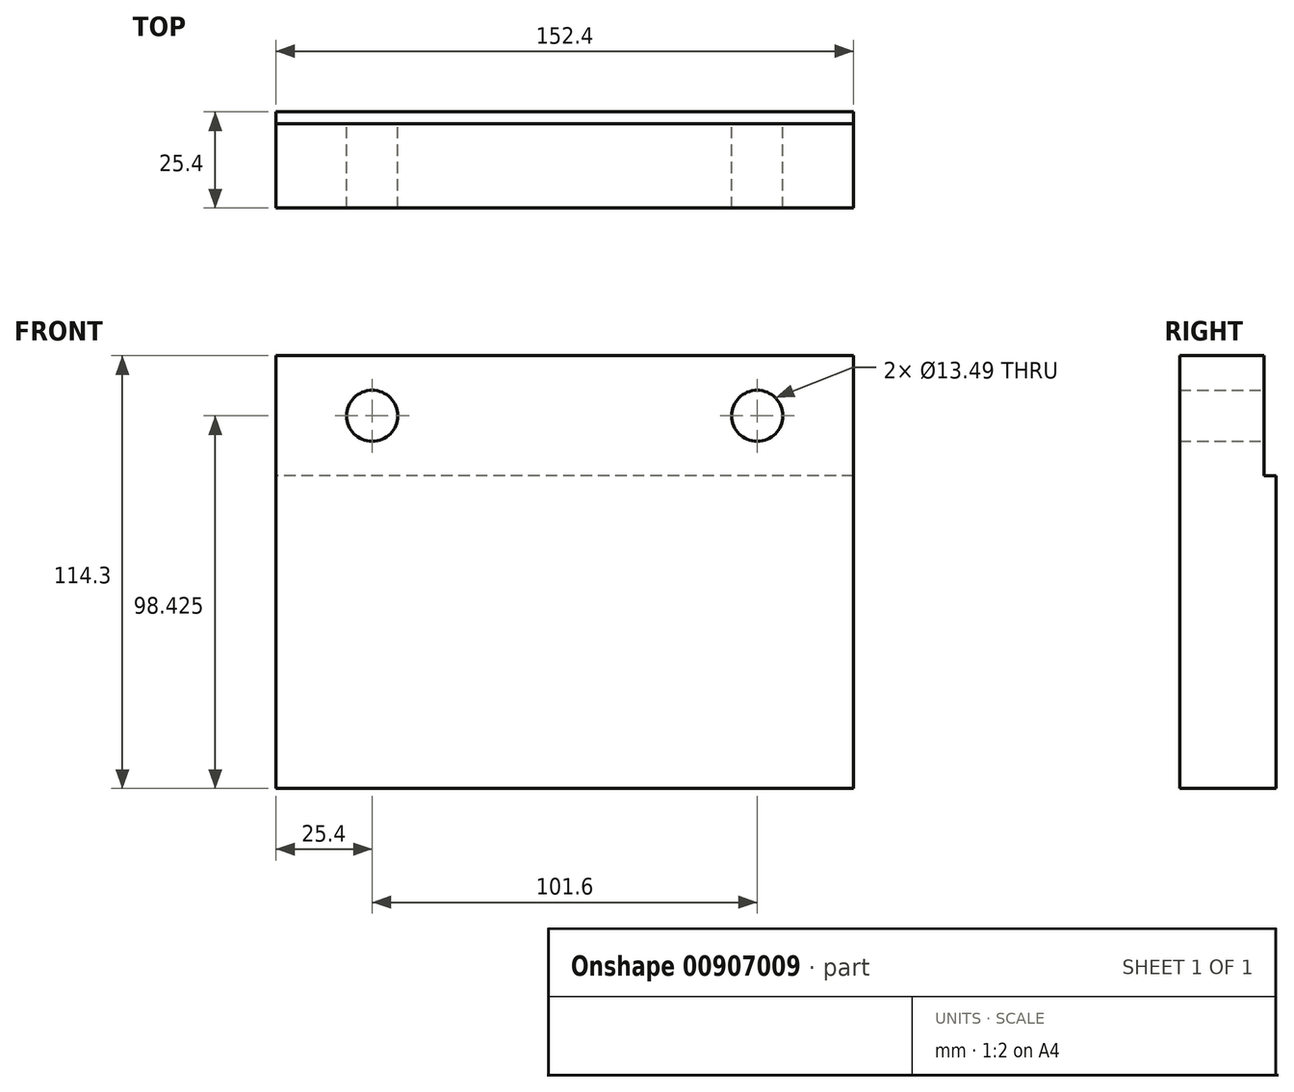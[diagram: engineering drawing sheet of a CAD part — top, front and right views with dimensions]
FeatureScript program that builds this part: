
annotation { "Feature Type Name" : "Feature", "Feature Type Description" : "" }
export const myFeature = defineFeature(function(context is Context, id is Id, definition is map)
    precondition{}
    {
        {
            var Q0;
            Q0=qCreatedBy(makeId("Front.planeOp"),FACE);
            var sketch = newSketch(context, id + "F0", { "sketchPlane" : qUnion([Q0])});
            skLineSegment(sketch, "E0.bottom", {"start": v(76.2, 57.15) * mm, "end": v(-76.2, 57.15) * mm});
            skLineSegment(sketch, "E0.top", {"start": v(76.2, -57.15) * mm, "end": v(-76.2, -57.15) * mm});
            skLineSegment(sketch, "E0.left", {"start": v(76.2, 57.15) * mm, "end": v(76.2, -57.15) * mm});
            skLineSegment(sketch, "E0.right", {"start": v(-76.2, 57.15) * mm, "end": v(-76.2, -57.15) * mm});
            skPoint(sketch, "E0.middle", {"position": v(0, 0) * mm});
            skSolve(sketch);
        }
        {
            var Q0;
            Q0=makeQuery(id+"F0.imprint","IMPRINT",FACE,{"disambiguationData":[TD([[makeQuery(id+"F0.imprint","IMPRINT",EDGE,{"derivedFrom":sQuery(id+"F0.wireOp",EDGE,"E0.bottom")}),1.0]])]});
            extrude(context, id + "F1", {"entities" : qUnion([Q0]), "depth" : 25.4 * mm, "offsetDistance" : 25.4 * mm});
        }
        {
            var Q0;
            Q0=makeQuery(id+"F1.opExtrude","CAP_FACE",FACE,{"disambiguationData":[OSD([sQuery(id+"F0.wireOp",EDGE,"E0.bottom"),sQuery(id+"F0.wireOp",EDGE,"E0.top"),sQuery(id+"F0.wireOp",EDGE,"E0.left"),sQuery(id+"F0.wireOp",EDGE,"E0.right")])],"isStart":true});
            var sketch = newSketch(context, id + "F2", { "sketchPlane" : qUnion([Q0])});
            skLineSegment(sketch, "E1.bottom", {"start": v(-76.2, 57.15) * mm, "end": v(76.2, 57.15) * mm});
            skLineSegment(sketch, "E1.top", {"start": v(-76.2, 25.4) * mm, "end": v(76.2, 25.4) * mm});
            skLineSegment(sketch, "E1.left", {"start": v(-76.2, 57.15) * mm, "end": v(-76.2, 25.4) * mm});
            skLineSegment(sketch, "E1.right", {"start": v(76.2, 57.15) * mm, "end": v(76.2, 25.4) * mm});
            skSolve(sketch);
        }
        {
            var Q0;
            Q0=makeQuery(id+"F2.imprint","IMPRINT",FACE,{"disambiguationData":[TD([[makeQuery(id+"F2.imprint","IMPRINT",EDGE,{"derivedFrom":sQuery(id+"F2.wireOp",EDGE,"E1.bottom")}),-1.0]])]});
            extrude(context, id + "F3", {"entities" : qUnion([Q0]), "operationType" : NewBodyOperationType.REMOVE, "oppositeDirection" : true, "depth" : 3.17 * mm, "offsetDistance" : 25.4 * mm});
        }
        {
            var Q0;
            Q0=makeQuery(id+"F3.boolean.opBoolean","COPY",FACE,{"derivedFrom":makeQuery(id+"F3.opExtrude","CAP_FACE",FACE,{"disambiguationData":[OSD([sQuery(id+"F2.wireOp",EDGE,"E1.bottom"),sQuery(id+"F2.wireOp",EDGE,"E1.top"),sQuery(id+"F2.wireOp",EDGE,"E1.left"),sQuery(id+"F2.wireOp",EDGE,"E1.right")])],"isStart":false})});
            var sketch = newSketch(context, id + "F4", { "sketchPlane" : qUnion([Q0])});
            skLineSegment(sketch, "E2", {"start": v(-50.8, 41.28) * mm, "end": v(50.8, 41.28) * mm, "construction": true});
            skLineSegment(sketch, "E3", {"start": v(0, 57.15) * mm, "end": v(0, 41.28) * mm, "construction": true});
            skSolve(sketch);
        }
        {
            var Q0;
            Q0=sQuery(id+"F4.wireOp",VERTEX,"E2.end");
            var Q1;
            Q1=sQuery(id+"F4.wireOp",VERTEX,"E2.start");
            var Q2;
            Q2=makeQuery(id+"F1.opExtrude","SWEPT_BODY",BODY,{"disambiguationData":[OSD([sQuery(id+"F0.wireOp",EDGE,"E0.bottom"),sQuery(id+"F0.wireOp",EDGE,"E0.top"),sQuery(id+"F0.wireOp",EDGE,"E0.left"),sQuery(id+"F0.wireOp",EDGE,"E0.right")])]});
            hole(context, id + "F5", {"style" : HoleStyle.SIMPLE, "endStyle" : HoleEndStyle.THROUGH, "standardTappedOrClearance" : lookupTablePath({ "fit" : "Free", "standard" : "ANSI", "size" : "1/2", "type" : "Clearance" }), "standardBlindInLast" : lookupTablePath({ "fit" : "Free", "standard" : "ANSI", "engagement" : "75%", "pitch" : "13 tpi", "size" : "1/2", "type" : "Clearance & tapped" }), "holeDiameter" : 13.5 * mm, "majorDiameter" : 12.7 * mm, "isTappedThrough" : true, "tappedDepth" : 12.7 * mm, "tapClearance" : 3, "locations" : qUnion([Q0, Q1]), "scope" : qUnion([Q2])});
        }
    });
